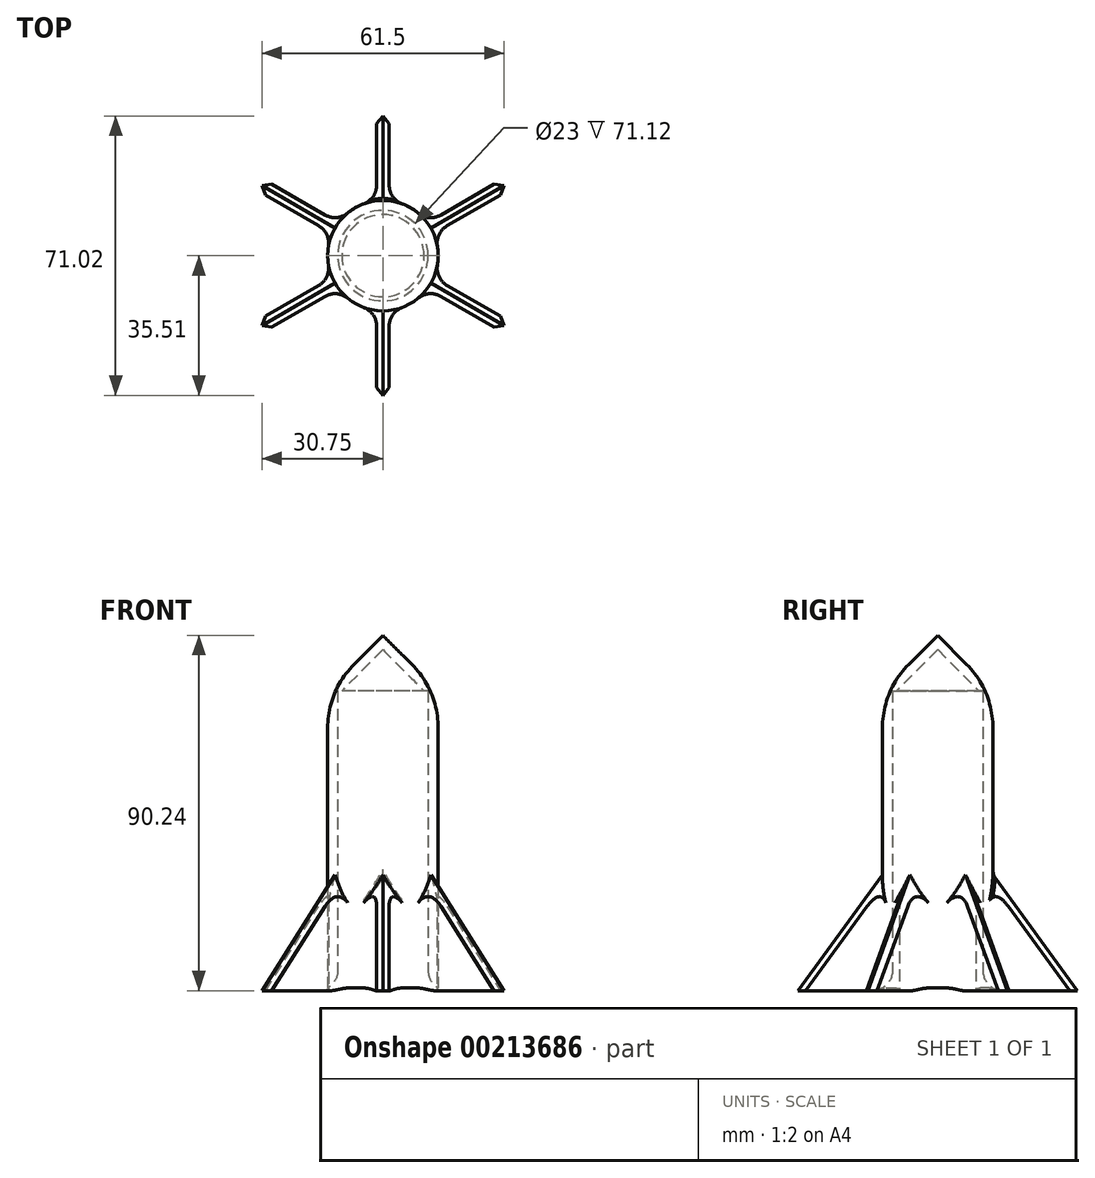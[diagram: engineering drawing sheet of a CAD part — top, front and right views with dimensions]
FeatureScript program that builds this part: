
annotation { "Feature Type Name" : "Feature", "Feature Type Description" : "" }
export const myFeature = defineFeature(function(context is Context, id is Id, definition is map)
    precondition{}
    {
        {
            var Q0;
            Q0=qCreatedBy(makeId("Top.planeOp"),FACE);
            var sketch = newSketch(context, id + "F0", { "sketchPlane" : qUnion([Q0])});
            skCircle(sketch, "E0", {"center": v(0, 0) * mm, "radius": 11.5 * mm});
            skCircle(sketch, "E1", {"center": v(0, 0) * mm, "radius": 14.04 * mm});
            skSolve(sketch);
        }
        {
            var Q0;
            Q0 = qSketchRegion(id + "F0", true);
            extrude(context, id + "F1", {"entities" : qUnion([Q0]), "depth" : 76.2 * mm});
        }
        {
            var Q0;
            Q0=makeQuery(id+"F1.opExtrude","CAP_FACE",FACE,{"disambiguationData":[OSD([sQuery(id+"F0.wireOp",EDGE,"E0"),sQuery(id+"F0.wireOp",EDGE,"E1")])],"isStart":false});
            var sketch = newSketch(context, id + "F2", { "sketchPlane" : qUnion([Q0])});
            skCircle(sketch, "E2.0", {"center": v(0, 0) * mm, "radius": 14.04 * mm});
            skSolve(sketch);
        }
        {
            var Q0;
            Q0 = qSketchRegion(id + "F2", true);
            extrude(context, id + "F3", {"entities" : qUnion([Q0]), "operationType" : NewBodyOperationType.ADD, "depth" : 25.4 * mm, "hasDraft" : true, "draftAngle" : 45 * degree, "draftPullDirection" : true});
        }
        {
            var Q0;
            Q0=makeQuery(id+"F3.opExtrude","CAP_FACE",FACE,{"disambiguationData":[OSD([sQuery(id+"F2.wireOp",EDGE,"E2.0")])],"isStart":true});
            shell(context, id + "F4", {"entities" : qUnion([Q0]), "thickness" : 2.54 * mm});
        }
        {
            var Q0;
            Q0=makeQuery(id+"F3.boolean.opBoolean","MERGE",EDGE,{"derivedFrom":[makeQuery(id+"F1.opExtrude","CAP_EDGE",EDGE,{"disambiguationData":[OSD([sQuery(id+"F0.wireOp",EDGE,"E1")])],"isStart":false}),makeQuery(id+"F3.opExtrude","CAP_EDGE",EDGE,{"disambiguationData":[OSD([sQuery(id+"F2.wireOp",EDGE,"E2.0")])],"isStart":true})]});
            fillet(context, id + "F5", {"entities" : qUnion([Q0]), "radius" : 22.86 * mm, "tangentPropagation" : true, "allowEdgeOverflow" : false});
        }
        {
            var Q0;
            Q0=qCreatedBy(makeId("Right.planeOp"),FACE);
            var sketch = newSketch(context, id + "F6", { "sketchPlane" : qUnion([Q0])});
            skLineSegment(sketch, "E3", {"start": v(-11.94, 0) * mm, "end": v(-11.94, 33.96) * mm});
            skLineSegment(sketch, "E4", {"start": v(-11.94, 33.96) * mm, "end": v(-36.69, 0) * mm});
            skLineSegment(sketch, "E5", {"start": v(-36.69, 0) * mm, "end": v(-11.94, 0) * mm});
            skSolve(sketch);
        }
        {
            var Q0;
            Q0 = qSketchRegion(id + "F6", true);
            extrude(context, id + "F7", {"entities" : qUnion([Q0]), "endBound" : BoundingType.SYMMETRIC, "depth" : 3.17 * mm});
        }
        {
            var Q0;
            Q0=makeQuery(id+"F7.opExtrude","CAP_EDGE",EDGE,{"disambiguationData":[OSD([sQuery(id+"F6.wireOp",EDGE,"E4")])],"isStart":true});
            var Q1;
            Q1=makeQuery(id+"F7.opExtrude","CAP_EDGE",EDGE,{"disambiguationData":[OSD([sQuery(id+"F6.wireOp",EDGE,"E4")])],"isStart":false});
            chamfer(context, id + "F8", {"entities" : qUnion([Q0, Q1]), "width" : 2.54 * mm, "tangentPropagation" : true});
        }
        {
            var Q0;
            Q0=makeQuery(id+"F7.opExtrude","SWEPT_BODY",BODY,{"disambiguationData":[OSD([sQuery(id+"F6.wireOp",EDGE,"E3"),sQuery(id+"F6.wireOp",EDGE,"E4"),sQuery(id+"F6.wireOp",EDGE,"E5")])]});
            var Q1;
            Q1=makeQuery(id+"F1.opExtrude","CAP_EDGE",EDGE,{"disambiguationData":[OSD([sQuery(id+"F0.wireOp",EDGE,"E1")])],"isStart":true});
            circularPattern(context, id + "F9", {"entities" : qUnion([Q0]), "axis" : qUnion([Q1]), "angle" : 360 * degree, "instanceCount" : 6, "equalSpace" : true});
        }
        {
            var Q0;
            Q0=makeQuery(id+"F9.opPattern","COPY",BODY,{"derivedFrom":makeQuery(id+"F7.opExtrude","SWEPT_BODY",BODY,{"disambiguationData":[OSD([sQuery(id+"F6.wireOp",EDGE,"E3"),sQuery(id+"F6.wireOp",EDGE,"E4"),sQuery(id+"F6.wireOp",EDGE,"E5")])]}),"instanceName":"5"});
            var Q1;
            Q1=makeQuery(id+"F1.opExtrude","SWEPT_BODY",BODY,{"disambiguationData":[OSD([sQuery(id+"F0.wireOp",EDGE,"E0"),sQuery(id+"F0.wireOp",EDGE,"E1")])]});
            var Q2;
            Q2=makeQuery(id+"F7.opExtrude","SWEPT_BODY",BODY,{"disambiguationData":[OSD([sQuery(id+"F6.wireOp",EDGE,"E3"),sQuery(id+"F6.wireOp",EDGE,"E4"),sQuery(id+"F6.wireOp",EDGE,"E5")])]});
            var Q3;
            Q3=makeQuery(id+"F9.opPattern","COPY",BODY,{"derivedFrom":makeQuery(id+"F7.opExtrude","SWEPT_BODY",BODY,{"disambiguationData":[OSD([sQuery(id+"F6.wireOp",EDGE,"E3"),sQuery(id+"F6.wireOp",EDGE,"E4"),sQuery(id+"F6.wireOp",EDGE,"E5")])]}),"instanceName":"3"});
            var Q4;
            Q4=makeQuery(id+"F9.opPattern","COPY",BODY,{"derivedFrom":makeQuery(id+"F7.opExtrude","SWEPT_BODY",BODY,{"disambiguationData":[OSD([sQuery(id+"F6.wireOp",EDGE,"E3"),sQuery(id+"F6.wireOp",EDGE,"E4"),sQuery(id+"F6.wireOp",EDGE,"E5")])]}),"instanceName":"1"});
            var Q5;
            Q5=makeQuery(id+"F9.opPattern","COPY",BODY,{"derivedFrom":makeQuery(id+"F7.opExtrude","SWEPT_BODY",BODY,{"disambiguationData":[OSD([sQuery(id+"F6.wireOp",EDGE,"E3"),sQuery(id+"F6.wireOp",EDGE,"E4"),sQuery(id+"F6.wireOp",EDGE,"E5")])]}),"instanceName":"4"});
            var Q6;
            Q6=makeQuery(id+"F9.opPattern","COPY",BODY,{"derivedFrom":makeQuery(id+"F7.opExtrude","SWEPT_BODY",BODY,{"disambiguationData":[OSD([sQuery(id+"F6.wireOp",EDGE,"E3"),sQuery(id+"F6.wireOp",EDGE,"E4"),sQuery(id+"F6.wireOp",EDGE,"E5")])]}),"instanceName":"2"});
            booleanBodies(context, id + "F10", {"operationType" : BooleanOperationType.UNION, "tools" : qUnion([Q0, Q1, Q2, Q3, Q4, Q5, Q6])});
        }
        {
            var Q0;
            Q0=makeQuery(id+"F10.opBoolean","INTERSECT",EDGE,{"derivedFrom":[makeQuery(id+"F1.opExtrude","SWEPT_FACE",FACE,{"disambiguationData":[OSD([sQuery(id+"F0.wireOp",EDGE,"E1")])]}),makeQuery(id+"F9.opPattern","COPY",FACE,{"derivedFrom":makeQuery(id+"F7.opExtrude","CAP_FACE",FACE,{"disambiguationData":[OSD([sQuery(id+"F6.wireOp",EDGE,"E3"),sQuery(id+"F6.wireOp",EDGE,"E4"),sQuery(id+"F6.wireOp",EDGE,"E5")])],"isStart":false}),"instanceName":"3"})]});
            var Q1;
            Q1=makeQuery(id+"F10.opBoolean","INTERSECT",EDGE,{"derivedFrom":[makeQuery(id+"F1.opExtrude","SWEPT_FACE",FACE,{"disambiguationData":[OSD([sQuery(id+"F0.wireOp",EDGE,"E1")])]}),makeQuery(id+"F9.opPattern","COPY",FACE,{"derivedFrom":makeQuery(id+"F7.opExtrude","CAP_FACE",FACE,{"disambiguationData":[OSD([sQuery(id+"F6.wireOp",EDGE,"E3"),sQuery(id+"F6.wireOp",EDGE,"E4"),sQuery(id+"F6.wireOp",EDGE,"E5")])],"isStart":true}),"instanceName":"4"})]});
            var Q2;
            Q2=makeQuery(id+"F10.opBoolean","INTERSECT",EDGE,{"derivedFrom":[makeQuery(id+"F1.opExtrude","SWEPT_FACE",FACE,{"disambiguationData":[OSD([sQuery(id+"F0.wireOp",EDGE,"E1")])]}),makeQuery(id+"F9.opPattern","COPY",FACE,{"derivedFrom":makeQuery(id+"F7.opExtrude","CAP_FACE",FACE,{"disambiguationData":[OSD([sQuery(id+"F6.wireOp",EDGE,"E3"),sQuery(id+"F6.wireOp",EDGE,"E4"),sQuery(id+"F6.wireOp",EDGE,"E5")])],"isStart":false}),"instanceName":"4"})]});
            var Q3;
            Q3=makeQuery(id+"F10.opBoolean","INTERSECT",EDGE,{"derivedFrom":[makeQuery(id+"F1.opExtrude","SWEPT_FACE",FACE,{"disambiguationData":[OSD([sQuery(id+"F0.wireOp",EDGE,"E1")])]}),makeQuery(id+"F9.opPattern","COPY",FACE,{"derivedFrom":makeQuery(id+"F7.opExtrude","CAP_FACE",FACE,{"disambiguationData":[OSD([sQuery(id+"F6.wireOp",EDGE,"E3"),sQuery(id+"F6.wireOp",EDGE,"E4"),sQuery(id+"F6.wireOp",EDGE,"E5")])],"isStart":true}),"instanceName":"5"})]});
            var Q4;
            Q4=makeQuery(id+"F10.opBoolean","INTERSECT",EDGE,{"derivedFrom":[makeQuery(id+"F1.opExtrude","SWEPT_FACE",FACE,{"disambiguationData":[OSD([sQuery(id+"F0.wireOp",EDGE,"E1")])]}),makeQuery(id+"F9.opPattern","COPY",FACE,{"derivedFrom":makeQuery(id+"F7.opExtrude","CAP_FACE",FACE,{"disambiguationData":[OSD([sQuery(id+"F6.wireOp",EDGE,"E3"),sQuery(id+"F6.wireOp",EDGE,"E4"),sQuery(id+"F6.wireOp",EDGE,"E5")])],"isStart":false}),"instanceName":"5"})]});
            var Q5;
            Q5=makeQuery(id+"F10.opBoolean","INTERSECT",EDGE,{"derivedFrom":[makeQuery(id+"F1.opExtrude","SWEPT_FACE",FACE,{"disambiguationData":[OSD([sQuery(id+"F0.wireOp",EDGE,"E1")])]}),makeQuery(id+"F7.opExtrude","CAP_FACE",FACE,{"disambiguationData":[OSD([sQuery(id+"F6.wireOp",EDGE,"E3"),sQuery(id+"F6.wireOp",EDGE,"E4"),sQuery(id+"F6.wireOp",EDGE,"E5")])],"isStart":true})]});
            var Q6;
            Q6=makeQuery(id+"F10.opBoolean","INTERSECT",EDGE,{"derivedFrom":[makeQuery(id+"F1.opExtrude","SWEPT_FACE",FACE,{"disambiguationData":[OSD([sQuery(id+"F0.wireOp",EDGE,"E1")])]}),makeQuery(id+"F7.opExtrude","CAP_FACE",FACE,{"disambiguationData":[OSD([sQuery(id+"F6.wireOp",EDGE,"E3"),sQuery(id+"F6.wireOp",EDGE,"E4"),sQuery(id+"F6.wireOp",EDGE,"E5")])],"isStart":false})]});
            var Q7;
            Q7=makeQuery(id+"F10.opBoolean","INTERSECT",EDGE,{"derivedFrom":[makeQuery(id+"F1.opExtrude","SWEPT_FACE",FACE,{"disambiguationData":[OSD([sQuery(id+"F0.wireOp",EDGE,"E1")])]}),makeQuery(id+"F9.opPattern","COPY",FACE,{"derivedFrom":makeQuery(id+"F7.opExtrude","CAP_FACE",FACE,{"disambiguationData":[OSD([sQuery(id+"F6.wireOp",EDGE,"E3"),sQuery(id+"F6.wireOp",EDGE,"E4"),sQuery(id+"F6.wireOp",EDGE,"E5")])],"isStart":true}),"instanceName":"1"})]});
            var Q8;
            Q8=makeQuery(id+"F10.opBoolean","INTERSECT",EDGE,{"derivedFrom":[makeQuery(id+"F1.opExtrude","SWEPT_FACE",FACE,{"disambiguationData":[OSD([sQuery(id+"F0.wireOp",EDGE,"E1")])]}),makeQuery(id+"F9.opPattern","COPY",FACE,{"derivedFrom":makeQuery(id+"F7.opExtrude","CAP_FACE",FACE,{"disambiguationData":[OSD([sQuery(id+"F6.wireOp",EDGE,"E3"),sQuery(id+"F6.wireOp",EDGE,"E4"),sQuery(id+"F6.wireOp",EDGE,"E5")])],"isStart":false}),"instanceName":"1"})]});
            var Q9;
            Q9=makeQuery(id+"F10.opBoolean","INTERSECT",EDGE,{"derivedFrom":[makeQuery(id+"F1.opExtrude","SWEPT_FACE",FACE,{"disambiguationData":[OSD([sQuery(id+"F0.wireOp",EDGE,"E1")])]}),makeQuery(id+"F9.opPattern","COPY",FACE,{"derivedFrom":makeQuery(id+"F7.opExtrude","CAP_FACE",FACE,{"disambiguationData":[OSD([sQuery(id+"F6.wireOp",EDGE,"E3"),sQuery(id+"F6.wireOp",EDGE,"E4"),sQuery(id+"F6.wireOp",EDGE,"E5")])],"isStart":true}),"instanceName":"2"})]});
            var Q10;
            Q10=makeQuery(id+"F10.opBoolean","INTERSECT",EDGE,{"derivedFrom":[makeQuery(id+"F1.opExtrude","SWEPT_FACE",FACE,{"disambiguationData":[OSD([sQuery(id+"F0.wireOp",EDGE,"E1")])]}),makeQuery(id+"F9.opPattern","COPY",FACE,{"derivedFrom":makeQuery(id+"F7.opExtrude","CAP_FACE",FACE,{"disambiguationData":[OSD([sQuery(id+"F6.wireOp",EDGE,"E3"),sQuery(id+"F6.wireOp",EDGE,"E4"),sQuery(id+"F6.wireOp",EDGE,"E5")])],"isStart":false}),"instanceName":"2"})]});
            var Q11;
            Q11=makeQuery(id+"F10.opBoolean","INTERSECT",EDGE,{"derivedFrom":[makeQuery(id+"F1.opExtrude","SWEPT_FACE",FACE,{"disambiguationData":[OSD([sQuery(id+"F0.wireOp",EDGE,"E1")])]}),makeQuery(id+"F9.opPattern","COPY",FACE,{"derivedFrom":makeQuery(id+"F7.opExtrude","CAP_FACE",FACE,{"disambiguationData":[OSD([sQuery(id+"F6.wireOp",EDGE,"E3"),sQuery(id+"F6.wireOp",EDGE,"E4"),sQuery(id+"F6.wireOp",EDGE,"E5")])],"isStart":true}),"instanceName":"3"})]});
            fillet(context, id + "F11", {"entities" : qUnion([Q0, Q1, Q2, Q3, Q4, Q5, Q6, Q7, Q8, Q9, Q10, Q11]), "radius" : 5.08 * mm, "tangentPropagation" : true, "allowEdgeOverflow" : false});
        }
        {
            var Q0;
            {var subQ0=sQuery(id+"F6.wireOp",EDGE,"E4");Q0=makeQuery(id+"F10.opBoolean","INTERSECT",EDGE,{"derivedFrom":[makeQuery(id+"F1.opExtrude","SWEPT_FACE",FACE,{"disambiguationData":[OSD([sQuery(id+"F0.wireOp",EDGE,"E1")])]}),makeQuery(id+"F9.opPattern","COPY",FACE,{"derivedFrom":makeQuery(id+"F8.opChamfer","BLEND_FACE",FACE,{"disambiguationData":[OSD([subQ0]),TDD([makeQuery(id+"F7.opExtrude","CAP_EDGE",EDGE,{"disambiguationData":[OSD([subQ0])],"isStart":true})])]}),"instanceName":"3"})]});}
            var Q1;
            {var subQ0=sQuery(id+"F6.wireOp",EDGE,"E4");Q1=makeQuery(id+"F10.opBoolean","INTERSECT",EDGE,{"derivedFrom":[makeQuery(id+"F1.opExtrude","SWEPT_FACE",FACE,{"disambiguationData":[OSD([sQuery(id+"F0.wireOp",EDGE,"E1")])]}),makeQuery(id+"F9.opPattern","COPY",FACE,{"derivedFrom":makeQuery(id+"F8.opChamfer","BLEND_FACE",FACE,{"disambiguationData":[OSD([subQ0]),TDD([makeQuery(id+"F7.opExtrude","CAP_EDGE",EDGE,{"disambiguationData":[OSD([subQ0])],"isStart":false})])]}),"instanceName":"3"})]});}
            fillet(context, id + "F12", {"entities" : qUnion([Q0, Q1]), "radius" : 1.27 * mm, "tangentPropagation" : true, "allowEdgeOverflow" : false});
        }
        {
            var Q0;
            Q0=makeQuery(id+"F1.opExtrude","CAP_EDGE",EDGE,{"disambiguationData":[OSD([sQuery(id+"F0.wireOp",EDGE,"E0")])],"isStart":true});
            fillet(context, id + "F13", {"entities" : qUnion([Q0]), "radius" : 5.08 * mm, "tangentPropagation" : true, "allowEdgeOverflow" : false});
        }
    });
